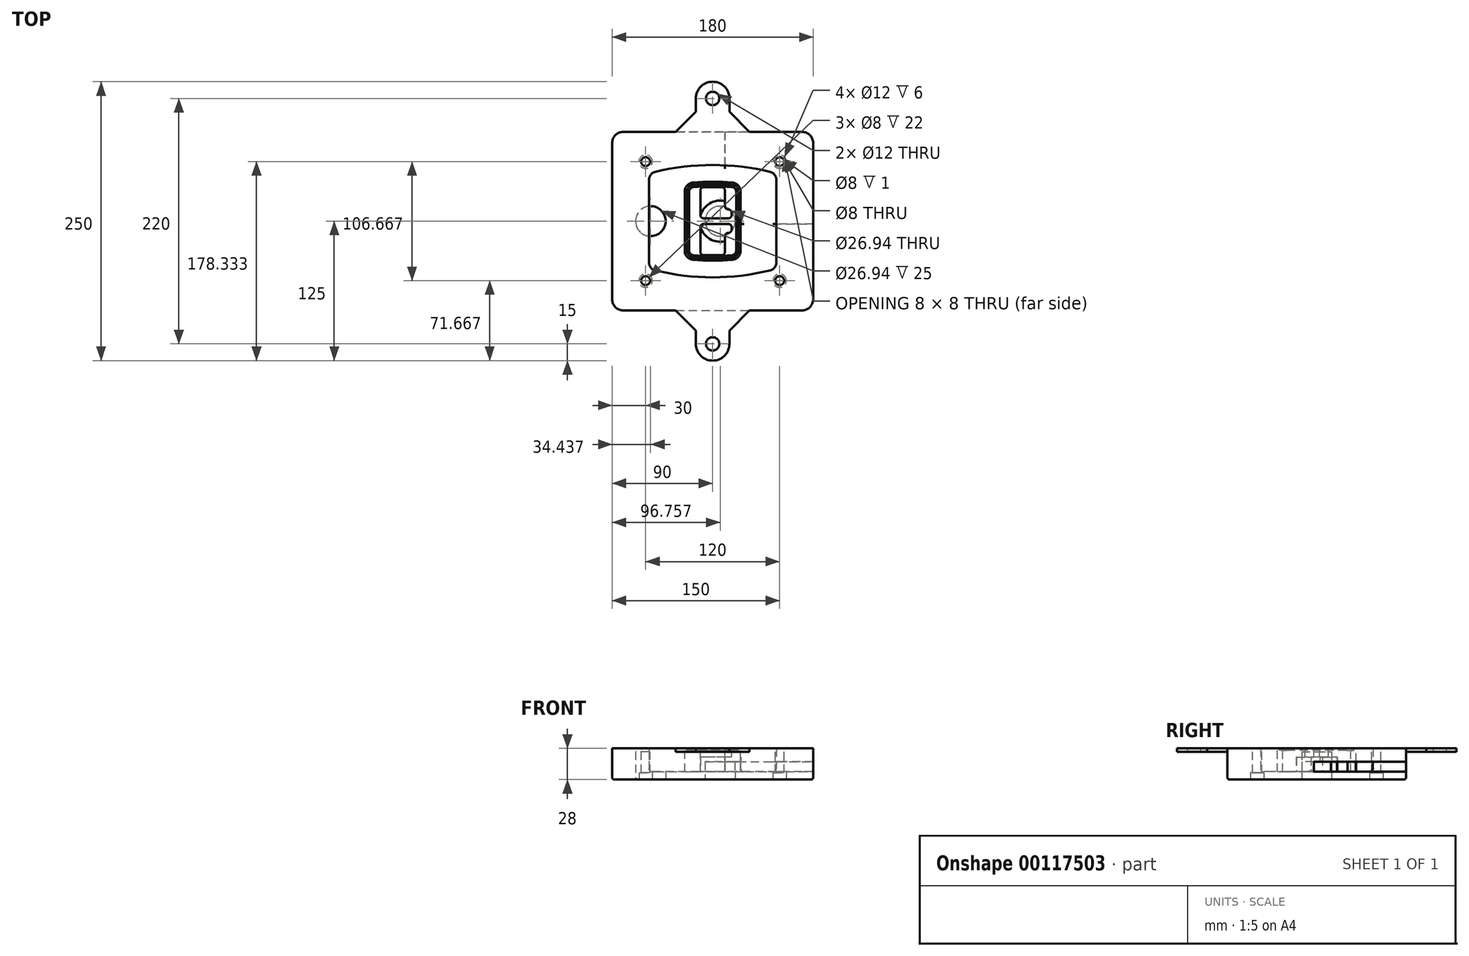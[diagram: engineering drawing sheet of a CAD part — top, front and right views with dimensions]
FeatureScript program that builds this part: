
annotation { "Feature Type Name" : "Feature", "Feature Type Description" : "" }
export const myFeature = defineFeature(function(context is Context, id is Id, definition is map)
    precondition{}
    {
        {
            var Q0;
            Q0=qCreatedBy(makeId("Top.planeOp"),FACE);
            var sketch = newSketch(context, id + "F0", { "sketchPlane" : qUnion([Q0])});
            skPoint(sketch, "E0.rect.middle", {"position": v(0, 0) * mm});
            skLineSegment(sketch, "E1.bottom", {"start": v(-80, -80) * mm, "end": v(80, -80) * mm});
            skLineSegment(sketch, "E1.top", {"start": v(-80, 80) * mm, "end": v(80, 80) * mm});
            skLineSegment(sketch, "E1.left", {"start": v(-90, -70) * mm, "end": v(-90, 70) * mm});
            skLineSegment(sketch, "E1.right", {"start": v(90, -70) * mm, "end": v(90, 70) * mm});
            skLineSegment(sketch, "E2", {"start": v(-90, 80) * mm, "end": v(90, -80) * mm, "construction": true});
            skLineSegment(sketch, "E3", {"start": v(90, 80) * mm, "end": v(-90, -80) * mm, "construction": true});
            skCircle(sketch, "E4", {"center": v(-60, 53.33) * mm, "radius": 4 * mm});
            skCircle(sketch, "E5", {"center": v(60, 53.33) * mm, "radius": 4 * mm});
            skCircle(sketch, "E6", {"center": v(60, -53.33) * mm, "radius": 4 * mm});
            skCircle(sketch, "E7", {"center": v(-60, -53.33) * mm, "radius": 4 * mm});
            skLineSegment(sketch, "E8", {"start": v(-60, 53.33) * mm, "end": v(60, 53.33) * mm, "construction": true});
            skLineSegment(sketch, "E9", {"start": v(60, 53.33) * mm, "end": v(60, -53.33) * mm, "construction": true});
            skLineSegment(sketch, "E10", {"start": v(60, -53.33) * mm, "end": v(-60, -53.33) * mm, "construction": true});
            skLineSegment(sketch, "E11", {"start": v(-60, -53.33) * mm, "end": v(-60, 53.33) * mm, "construction": true});
            skLineSegment(sketch, "E12", {"start": v(-60, 37.3) * mm, "end": v(-60, -37.3) * mm});
            skLineSegment(sketch, "E13", {"start": v(60, 37.3) * mm, "end": v(60, -37.3) * mm});
            skArc(sketch, "E14", {"start": v(52.38, 47.01) * mm, "mid": v(0, 53.33) * mm, "end": v(-52.38, 47.01) * mm});
            skArc(sketch, "E15", {"start": v(-52.38, -47.01) * mm, "mid": v(0, -53.33) * mm, "end": v(52.38, -47.01) * mm});
            skLineSegment(sketch, "E16", {"start": v(-60, 0) * mm, "end": v(60, 0) * mm, "construction": true});
            skPoint(sketch, "E17.visualSharp", {"position": v(-60, -45) * mm});
            skArc(sketch, "E17.filletArc", {"start": v(-60, -37.3) * mm, "mid": v(-57.87, -43.47) * mm, "end": v(-52.38, -47.01) * mm});
            skPoint(sketch, "E18.visualSharp", {"position": v(-60, 45) * mm});
            skArc(sketch, "E18.filletArc", {"start": v(-52.38, 47.01) * mm, "mid": v(-57.87, 43.47) * mm, "end": v(-60, 37.3) * mm});
            skPoint(sketch, "E19.visualSharp", {"position": v(60, 45) * mm});
            skArc(sketch, "E19.filletArc", {"start": v(60, 37.3) * mm, "mid": v(57.87, 43.47) * mm, "end": v(52.38, 47.01) * mm});
            skPoint(sketch, "E20.visualSharp", {"position": v(60, -45) * mm});
            skArc(sketch, "E20.filletArc", {"start": v(52.38, -47.01) * mm, "mid": v(57.87, -43.47) * mm, "end": v(60, -37.3) * mm});
            skPoint(sketch, "E21.visualSharp", {"position": v(-90, 80) * mm});
            skArc(sketch, "E21.filletArc", {"start": v(-80, 80) * mm, "mid": v(-87.07, 77.07) * mm, "end": v(-90, 70) * mm});
            skPoint(sketch, "E22.visualSharp", {"position": v(90, 80) * mm});
            skArc(sketch, "E22.filletArc", {"start": v(90, 70) * mm, "mid": v(87.07, 77.07) * mm, "end": v(80, 80) * mm});
            skPoint(sketch, "E23.visualSharp", {"position": v(90, -80) * mm});
            skArc(sketch, "E23.filletArc", {"start": v(80, -80) * mm, "mid": v(87.07, -77.07) * mm, "end": v(90, -70) * mm});
            skPoint(sketch, "E24.visualSharp", {"position": v(-90, -80) * mm});
            skArc(sketch, "E24.filletArc", {"start": v(-90, -70) * mm, "mid": v(-87.07, -77.07) * mm, "end": v(-80, -80) * mm});
            skArc(sketch, "E25.0", {"start": v(57, 37.3) * mm, "mid": v(55.5, 41.62) * mm, "end": v(51.67, 44.1) * mm});
            skLineSegment(sketch, "E25.1", {"start": v(57, 37.3) * mm, "end": v(57, -37.3) * mm});
            skArc(sketch, "E25.2", {"start": v(51.67, -44.1) * mm, "mid": v(55.5, -41.62) * mm, "end": v(57, -37.3) * mm});
            skArc(sketch, "E25.3", {"start": v(-51.67, -44.1) * mm, "mid": v(0, -50.33) * mm, "end": v(51.67, -44.1) * mm});
            skArc(sketch, "E25.4", {"start": v(-57, -37.3) * mm, "mid": v(-55.5, -41.62) * mm, "end": v(-51.67, -44.1) * mm});
            skArc(sketch, "E25.5", {"start": v(51.67, 44.1) * mm, "mid": v(0, 50.33) * mm, "end": v(-51.67, 44.1) * mm});
            skLineSegment(sketch, "E25.6", {"start": v(-57, 37.3) * mm, "end": v(-57, -37.3) * mm});
            skArc(sketch, "E25.7", {"start": v(-51.67, 44.1) * mm, "mid": v(-55.5, 41.62) * mm, "end": v(-57, 37.3) * mm});
            skArc(sketch, "E26.0", {"start": v(-53.33, 50.9) * mm, "mid": v(-61.01, 45.94) * mm, "end": v(-64, 37.3) * mm});
            skArc(sketch, "E26.1", {"start": v(53.33, 50.9) * mm, "mid": v(0, 57.33) * mm, "end": v(-53.33, 50.9) * mm});
            skArc(sketch, "E26.2", {"start": v(64, 37.3) * mm, "mid": v(61.01, 45.94) * mm, "end": v(53.33, 50.9) * mm});
            skLineSegment(sketch, "E26.3", {"start": v(64, 37.3) * mm, "end": v(64, -37.3) * mm});
            skArc(sketch, "E26.4", {"start": v(53.33, -50.9) * mm, "mid": v(61.01, -45.94) * mm, "end": v(64, -37.3) * mm});
            skLineSegment(sketch, "E26.5", {"start": v(-64, 37.3) * mm, "end": v(-64, -37.3) * mm});
            skArc(sketch, "E26.6", {"start": v(-53.33, -50.9) * mm, "mid": v(0, -57.33) * mm, "end": v(53.33, -50.9) * mm});
            skArc(sketch, "E26.7", {"start": v(-64, -37.3) * mm, "mid": v(-61.01, -45.94) * mm, "end": v(-53.33, -50.9) * mm});
            skSolve(sketch);
        }
        {
            var Q0;
            Q0=makeQuery(id+"F0.imprint","IMPRINT",FACE,{"disambiguationData":[TD([[makeQuery(id+"F0.imprint","IMPRINT",EDGE,{"derivedFrom":sQuery(id+"F0.wireOp",EDGE,"E1.bottom")}),1.0]])]});
            var Q1;
            Q1=makeQuery(id+"F0.imprint","IMPRINT",FACE,{"disambiguationData":[TD([[makeQuery(id+"F0.imprint","IMPRINT",EDGE,{"derivedFrom":sQuery(id+"F0.wireOp",EDGE,"E12")}),1.0]])]});
            var Q2;
            Q2=makeQuery(id+"F0.imprint","IMPRINT",FACE,{"disambiguationData":[TD([[makeQuery(id+"F0.imprint","IMPRINT",EDGE,{"derivedFrom":sQuery(id+"F0.wireOp",EDGE,"E25.0")}),1.0]])]});
            var Q3;
            Q3=makeQuery(id+"F0.imprint","IMPRINT",FACE,{"disambiguationData":[TD([[makeQuery(id+"F0.imprint","IMPRINT",EDGE,{"derivedFrom":sQuery(id+"F0.wireOp",EDGE,"E12")}),-1.0]])]});
            extrude(context, id + "F1", {"entities" : qUnion([Q0, Q1, Q2, Q3]), "oppositeDirection" : true, "depth" : 25 * mm});
        }
        {
            var Q0;
            Q0=makeQuery(id+"F0.imprint","IMPRINT",FACE,{"disambiguationData":[TD([[makeQuery(id+"F0.imprint","IMPRINT",EDGE,{"derivedFrom":sQuery(id+"F0.wireOp",EDGE,"E12")}),1.0]])]});
            extrude(context, id + "F2", {"entities" : qUnion([Q0]), "operationType" : NewBodyOperationType.ADD, "depth" : 3 * mm});
        }
        {
            var Q0;
            Q0=makeQuery(id+"F0.imprint","IMPRINT",FACE,{"disambiguationData":[TD([[makeQuery(id+"F0.imprint","IMPRINT",EDGE,{"derivedFrom":sQuery(id+"F0.wireOp",EDGE,"E25.0")}),1.0]])]});
            extrude(context, id + "F3", {"entities" : qUnion([Q0]), "operationType" : NewBodyOperationType.REMOVE, "oppositeDirection" : true, "depth" : 18 * mm});
        }
        {
            var Q0;
            Q0=makeQuery(id+"F2.opExtrude","CAP_FACE",FACE,{"disambiguationData":[OSD([sQuery(id+"F0.wireOp",EDGE,"E12"),sQuery(id+"F0.wireOp",EDGE,"E13"),sQuery(id+"F0.wireOp",EDGE,"E14"),sQuery(id+"F0.wireOp",EDGE,"E15"),sQuery(id+"F0.wireOp",EDGE,"E17.filletArc"),sQuery(id+"F0.wireOp",EDGE,"E18.filletArc"),sQuery(id+"F0.wireOp",EDGE,"E19.filletArc"),sQuery(id+"F0.wireOp",EDGE,"E20.filletArc"),sQuery(id+"F0.wireOp",EDGE,"E25.0"),sQuery(id+"F0.wireOp",EDGE,"E25.1"),sQuery(id+"F0.wireOp",EDGE,"E25.2"),sQuery(id+"F0.wireOp",EDGE,"E25.3"),sQuery(id+"F0.wireOp",EDGE,"E25.4"),sQuery(id+"F0.wireOp",EDGE,"E25.5"),sQuery(id+"F0.wireOp",EDGE,"E25.6"),sQuery(id+"F0.wireOp",EDGE,"E25.7")])],"isStart":false});
            var sketch = newSketch(context, id + "F4", { "sketchPlane" : qUnion([Q0])});
            skArc(sketch, "E27.0", {"start": v(-17.7, -34.56) * mm, "mid": v(0, -35.33) * mm, "end": v(17.7, -34.56) * mm});
            skArc(sketch, "E28.0", {"start": v(17.7, 34.56) * mm, "mid": v(0, 35.33) * mm, "end": v(-17.7, 34.56) * mm});
            skLineSegment(sketch, "E29", {"start": v(-25, 26.59) * mm, "end": v(-25, -26.59) * mm});
            skLineSegment(sketch, "E30", {"start": v(25, 26.59) * mm, "end": v(25, -26.59) * mm});
            skLineSegment(sketch, "E31", {"start": v(-25, 33.78) * mm, "end": v(25, 33.78) * mm, "construction": true});
            skLineSegment(sketch, "E32", {"start": v(-25, -33.78) * mm, "end": v(25, -33.78) * mm, "construction": true});
            skPoint(sketch, "E33.visualSharp", {"position": v(-25, 33.78) * mm});
            skArc(sketch, "E33.filletArc", {"start": v(-17.7, 34.56) * mm, "mid": v(-22.9, 32) * mm, "end": v(-25, 26.59) * mm});
            skPoint(sketch, "E34.visualSharp", {"position": v(25, 33.78) * mm});
            skArc(sketch, "E34.filletArc", {"start": v(25, 26.59) * mm, "mid": v(22.9, 32) * mm, "end": v(17.7, 34.56) * mm});
            skPoint(sketch, "E35.visualSharp", {"position": v(25, -33.78) * mm});
            skArc(sketch, "E35.filletArc", {"start": v(17.7, -34.56) * mm, "mid": v(22.9, -32) * mm, "end": v(25, -26.59) * mm});
            skPoint(sketch, "E36.visualSharp", {"position": v(-25, -33.78) * mm});
            skArc(sketch, "E36.filletArc", {"start": v(-25, -26.59) * mm, "mid": v(-22.9, -32) * mm, "end": v(-17.7, -34.56) * mm});
            skArc(sketch, "E37.0", {"start": v(51.67, 44.1) * mm, "mid": v(0, 50.33) * mm, "end": v(-51.67, 44.1) * mm});
            skArc(sketch, "E37.1", {"start": v(-51.67, 44.1) * mm, "mid": v(-55.5, 41.62) * mm, "end": v(-57, 37.3) * mm});
            skLineSegment(sketch, "E37.2", {"start": v(-57, 37.3) * mm, "end": v(-57, -37.3) * mm});
            skArc(sketch, "E37.3", {"start": v(-57, -37.3) * mm, "mid": v(-55.5, -41.62) * mm, "end": v(-51.67, -44.1) * mm});
            skArc(sketch, "E37.4", {"start": v(-51.67, -44.1) * mm, "mid": v(0, -50.33) * mm, "end": v(51.67, -44.1) * mm});
            skArc(sketch, "E37.5", {"start": v(51.67, -44.1) * mm, "mid": v(55.5, -41.62) * mm, "end": v(57, -37.3) * mm});
            skLineSegment(sketch, "E37.6", {"start": v(57, 37.3) * mm, "end": v(57, -37.3) * mm});
            skArc(sketch, "E37.7", {"start": v(57, 37.3) * mm, "mid": v(55.5, 41.62) * mm, "end": v(51.67, 44.1) * mm});
            skLineSegment(sketch, "E38.0", {"start": v(23, 26.59) * mm, "end": v(23, -26.59) * mm});
            skArc(sketch, "E38.1", {"start": v(17.53, -32.56) * mm, "mid": v(21.42, -30.64) * mm, "end": v(23, -26.59) * mm});
            skArc(sketch, "E38.2", {"start": v(-17.53, -32.56) * mm, "mid": v(0, -33.33) * mm, "end": v(17.53, -32.56) * mm});
            skArc(sketch, "E38.3", {"start": v(-23, -26.59) * mm, "mid": v(-21.42, -30.64) * mm, "end": v(-17.53, -32.56) * mm});
            skLineSegment(sketch, "E38.4", {"start": v(-23, 26.59) * mm, "end": v(-23, -26.59) * mm});
            skArc(sketch, "E38.5", {"start": v(23, 26.59) * mm, "mid": v(21.42, 30.64) * mm, "end": v(17.53, 32.56) * mm});
            skArc(sketch, "E38.6", {"start": v(-17.53, 32.56) * mm, "mid": v(-21.42, 30.64) * mm, "end": v(-23, 26.59) * mm});
            skArc(sketch, "E38.7", {"start": v(17.53, 32.56) * mm, "mid": v(0, 33.33) * mm, "end": v(-17.53, 32.56) * mm});
            skArc(sketch, "E39.0", {"start": v(21, 26.59) * mm, "mid": v(19.95, 29.29) * mm, "end": v(17.35, 30.57) * mm});
            skLineSegment(sketch, "E39.1", {"start": v(21, 26.59) * mm, "end": v(21, -26.59) * mm});
            skArc(sketch, "E39.2", {"start": v(17.35, -30.57) * mm, "mid": v(19.95, -29.29) * mm, "end": v(21, -26.59) * mm});
            skArc(sketch, "E39.3", {"start": v(-17.35, -30.57) * mm, "mid": v(0, -31.33) * mm, "end": v(17.35, -30.57) * mm});
            skArc(sketch, "E39.4", {"start": v(-21, -26.59) * mm, "mid": v(-19.95, -29.29) * mm, "end": v(-17.35, -30.57) * mm});
            skArc(sketch, "E39.5", {"start": v(17.35, 30.57) * mm, "mid": v(0, 31.33) * mm, "end": v(-17.35, 30.57) * mm});
            skLineSegment(sketch, "E39.6", {"start": v(-21, 26.59) * mm, "end": v(-21, -26.59) * mm});
            skArc(sketch, "E39.7", {"start": v(-17.35, 30.57) * mm, "mid": v(-19.95, 29.29) * mm, "end": v(-21, 26.59) * mm});
            skLineSegment(sketch, "E40", {"start": v(-25, 0) * mm, "end": v(25, 0) * mm, "construction": true});
            skLineSegment(sketch, "E41", {"start": v(-11, 5.5) * mm, "end": v(-11, 27.5) * mm});
            skLineSegment(sketch, "E42", {"start": v(-8, 30.5) * mm, "end": v(8, 30.5) * mm});
            skLineSegment(sketch, "E43", {"start": v(11, 27.5) * mm, "end": v(11, 13.5) * mm});
            skLineSegment(sketch, "E44", {"start": v(14, 10.5) * mm, "end": v(14, 10.5) * mm});
            skLineSegment(sketch, "E45", {"start": v(17, 7.5) * mm, "end": v(17, 5.5) * mm});
            skLineSegment(sketch, "E46", {"start": v(14, 2.5) * mm, "end": v(-8, 2.5) * mm});
            skPoint(sketch, "E47.visualSharp", {"position": v(-11, 30.5) * mm});
            skArc(sketch, "E47.filletArc", {"start": v(-8, 30.5) * mm, "mid": v(-10.12, 29.62) * mm, "end": v(-11, 27.5) * mm});
            skPoint(sketch, "E48.visualSharp", {"position": v(11, 30.5) * mm});
            skArc(sketch, "E48.filletArc", {"start": v(11, 27.5) * mm, "mid": v(10.12, 29.62) * mm, "end": v(8, 30.5) * mm});
            skPoint(sketch, "E49.visualSharp", {"position": v(11, 10.5) * mm});
            skArc(sketch, "E49.filletArc", {"start": v(11, 13.5) * mm, "mid": v(11.88, 11.38) * mm, "end": v(14, 10.5) * mm});
            skPoint(sketch, "E50.visualSharp", {"position": v(17, 10.5) * mm});
            skArc(sketch, "E50.filletArc", {"start": v(17, 7.5) * mm, "mid": v(16.12, 9.62) * mm, "end": v(14, 10.5) * mm});
            skPoint(sketch, "E51.visualSharp", {"position": v(17, 2.5) * mm});
            skArc(sketch, "E51.filletArc", {"start": v(14, 2.5) * mm, "mid": v(16.12, 3.38) * mm, "end": v(17, 5.5) * mm});
            skPoint(sketch, "E52.visualSharp", {"position": v(-11, 2.5) * mm});
            skArc(sketch, "E52.filletArc", {"start": v(-11, 5.5) * mm, "mid": v(-10.12, 3.38) * mm, "end": v(-8, 2.5) * mm});
            skLineSegment(sketch, "E53.0.MirrorCS", {"start": v(14, -2.5) * mm, "end": v(-8, -2.5) * mm});
            skArc(sketch, "E54.0.MirrorCS", {"start": v(-11, -5.5) * mm, "mid": v(-10.12, -3.38) * mm, "end": v(-8, -2.5) * mm});
            skLineSegment(sketch, "E55.0.MirrorCS", {"start": v(-11, -5.5) * mm, "end": v(-11, -27.5) * mm});
            skArc(sketch, "E56.0.MirrorCS", {"start": v(-8, -30.5) * mm, "mid": v(-10.12, -29.62) * mm, "end": v(-11, -27.5) * mm});
            skLineSegment(sketch, "E57.0.MirrorCS", {"start": v(-8, -30.5) * mm, "end": v(8, -30.5) * mm});
            skArc(sketch, "E58.0.MirrorCS", {"start": v(11, -27.5) * mm, "mid": v(10.12, -29.62) * mm, "end": v(8, -30.5) * mm});
            skLineSegment(sketch, "E59.0.MirrorCS", {"start": v(11, -27.5) * mm, "end": v(11, -13.5) * mm});
            skArc(sketch, "E60.0.MirrorCS", {"start": v(11, -13.5) * mm, "mid": v(11.88, -11.38) * mm, "end": v(14, -10.5) * mm});
            skArc(sketch, "E61.0.MirrorCS", {"start": v(17, -7.5) * mm, "mid": v(16.12, -9.62) * mm, "end": v(14, -10.5) * mm});
            skLineSegment(sketch, "E62.0.MirrorCS", {"start": v(17, -7.5) * mm, "end": v(17, -5.5) * mm});
            skArc(sketch, "E63.0.MirrorCS", {"start": v(14, -2.5) * mm, "mid": v(16.12, -3.38) * mm, "end": v(17, -5.5) * mm});
            skSolve(sketch);
        }
        {
            var Q0;
            Q0=makeQuery(id+"F4.imprint","IMPRINT",FACE,{"disambiguationData":[TD([[makeQuery(id+"F4.imprint","IMPRINT",EDGE,{"derivedFrom":sQuery(id+"F4.wireOp",EDGE,"E27.0")}),1.0]])]});
            var Q1;
            Q1=makeQuery(id+"F4.imprint","IMPRINT",FACE,{"disambiguationData":[TD([[makeQuery(id+"F4.imprint","IMPRINT",EDGE,{"derivedFrom":sQuery(id+"F4.wireOp",EDGE,"E38.0")}),-1.0]])]});
            var Q2;
            Q2=makeQuery(id+"F4.imprint","IMPRINT",FACE,{"disambiguationData":[TD([[makeQuery(id+"F4.imprint","IMPRINT",EDGE,{"derivedFrom":sQuery(id+"F4.wireOp",EDGE,"E39.0")}),1.0]])]});
            extrude(context, id + "F5", {"entities" : qUnion([Q0, Q1, Q2]), "operationType" : NewBodyOperationType.ADD, "endBound" : BoundingType.UP_TO_NEXT, "oppositeDirection" : true, "depth" : 25 * mm});
        }
        {
            var Q0;
            Q0=makeQuery(id+"F4.imprint","IMPRINT",FACE,{"disambiguationData":[TD([[makeQuery(id+"F4.imprint","IMPRINT",EDGE,{"derivedFrom":sQuery(id+"F4.wireOp",EDGE,"E38.0")}),-1.0]])]});
            extrude(context, id + "F6", {"entities" : qUnion([Q0]), "operationType" : NewBodyOperationType.REMOVE, "oppositeDirection" : true, "depth" : 2 * mm});
        }
        {
            var Q0;
            Q0=makeQuery(id+"F1.opExtrude","CAP_FACE",FACE,{"disambiguationData":[OSD([sQuery(id+"F0.wireOp",EDGE,"E1.bottom"),sQuery(id+"F0.wireOp",EDGE,"E1.top"),sQuery(id+"F0.wireOp",EDGE,"E1.left"),sQuery(id+"F0.wireOp",EDGE,"E1.right"),sQuery(id+"F0.wireOp",EDGE,"E4"),sQuery(id+"F0.wireOp",EDGE,"E5"),sQuery(id+"F0.wireOp",EDGE,"E6"),sQuery(id+"F0.wireOp",EDGE,"E7"),sQuery(id+"F0.wireOp",EDGE,"E21.filletArc"),sQuery(id+"F0.wireOp",EDGE,"E22.filletArc"),sQuery(id+"F0.wireOp",EDGE,"E23.filletArc"),sQuery(id+"F0.wireOp",EDGE,"E24.filletArc")])],"isStart":false});
            var sketch = newSketch(context, id + "F7", { "sketchPlane" : qUnion([Q0])});
            skCircle(sketch, "E64", {"center": v(6.76, 0) * mm, "radius": 13.47 * mm});
            skCircle(sketch, "E65", {"center": v(-55.56, 0) * mm, "radius": 13.47 * mm});
            skLineSegment(sketch, "E66", {"start": v(90, 0) * mm, "end": v(-90, 0) * mm});
            skCircle(sketch, "E67", {"center": v(6.76, 0) * mm, "radius": 18.47 * mm});
            skCircle(sketch, "E68", {"center": v(60, -53.33) * mm, "radius": 6 * mm});
            skCircle(sketch, "E69", {"center": v(-60, -53.33) * mm, "radius": 6 * mm});
            skCircle(sketch, "E70", {"center": v(-60, 53.33) * mm, "radius": 6 * mm});
            skCircle(sketch, "E71", {"center": v(60, 53.33) * mm, "radius": 6 * mm});
            skSolve(sketch);
        }
        {
            var Q0;
            {var subQ1=sQuery(id+"F7.wireOp",EDGE,"E66");var subQ4=sQuery(id+"F7.wireOp",EDGE,"E64");var subQ6=makeQuery(id+"F7.imprint","INTERSECT",VERTEX,{"disambiguationData":[OD(0.0)],"derivedFrom":[subQ4,subQ1]});Q0=makeQuery(id+"F7.imprint","IMPRINT",FACE,{"disambiguationData":[TD([[makeQuery(id+"F7.imprint","IMPRINT",EDGE,{"disambiguationData":[TD([[subQ6,-1.0]])],"derivedFrom":subQ4}),-1.0]])]});}
            var Q1;
            {var subQ0=sQuery(id+"F7.wireOp",EDGE,"E66");var subQ1=sQuery(id+"F7.wireOp",EDGE,"E64");var subQ3=makeQuery(id+"F7.imprint","INTERSECT",VERTEX,{"disambiguationData":[OD(0.0)],"derivedFrom":[subQ1,subQ0]});Q1=makeQuery(id+"F7.imprint","IMPRINT",FACE,{"disambiguationData":[TD([[makeQuery(id+"F7.imprint","IMPRINT",EDGE,{"disambiguationData":[TD([[subQ3,-1.0]])],"derivedFrom":subQ1}),1.0]])]});}
            var Q2;
            {var subQ0=sQuery(id+"F7.wireOp",EDGE,"E66");var subQ1=sQuery(id+"F7.wireOp",EDGE,"E64");var subQ3=makeQuery(id+"F7.imprint","INTERSECT",VERTEX,{"disambiguationData":[OD(0.0)],"derivedFrom":[subQ1,subQ0]});Q2=makeQuery(id+"F7.imprint","IMPRINT",FACE,{"disambiguationData":[TD([[makeQuery(id+"F7.imprint","IMPRINT",EDGE,{"disambiguationData":[TD([[subQ3,1.0]])],"derivedFrom":subQ1}),1.0]])]});}
            var Q3;
            {var subQ1=sQuery(id+"F7.wireOp",EDGE,"E66");var subQ4=sQuery(id+"F7.wireOp",EDGE,"E64");var subQ6=makeQuery(id+"F7.imprint","INTERSECT",VERTEX,{"disambiguationData":[OD(0.0)],"derivedFrom":[subQ4,subQ1]});Q3=makeQuery(id+"F7.imprint","IMPRINT",FACE,{"disambiguationData":[TD([[makeQuery(id+"F7.imprint","IMPRINT",EDGE,{"disambiguationData":[TD([[subQ6,1.0]])],"derivedFrom":subQ4}),-1.0]])]});}
            extrude(context, id + "F8", {"entities" : qUnion([Q0, Q1, Q2, Q3]), "operationType" : NewBodyOperationType.ADD, "oppositeDirection" : true, "depth" : 20 * mm});
        }
        {
            var Q0;
            {var subQ0=sQuery(id+"F7.wireOp",EDGE,"E66");var subQ1=sQuery(id+"F7.wireOp",EDGE,"E64");var subQ3=makeQuery(id+"F7.imprint","INTERSECT",VERTEX,{"disambiguationData":[OD(0.0)],"derivedFrom":[subQ1,subQ0]});Q0=makeQuery(id+"F7.imprint","IMPRINT",FACE,{"disambiguationData":[TD([[makeQuery(id+"F7.imprint","IMPRINT",EDGE,{"disambiguationData":[TD([[subQ3,-1.0]])],"derivedFrom":subQ1}),1.0]])]});}
            var Q1;
            {var subQ0=sQuery(id+"F7.wireOp",EDGE,"E66");var subQ1=sQuery(id+"F7.wireOp",EDGE,"E64");var subQ3=makeQuery(id+"F7.imprint","INTERSECT",VERTEX,{"disambiguationData":[OD(0.0)],"derivedFrom":[subQ1,subQ0]});Q1=makeQuery(id+"F7.imprint","IMPRINT",FACE,{"disambiguationData":[TD([[makeQuery(id+"F7.imprint","IMPRINT",EDGE,{"disambiguationData":[TD([[subQ3,1.0]])],"derivedFrom":subQ1}),1.0]])]});}
            extrude(context, id + "F9", {"entities" : qUnion([Q0, Q1]), "operationType" : NewBodyOperationType.REMOVE, "oppositeDirection" : true, "depth" : 16 * mm});
        }
        {
            var Q0;
            {var subQ0=sQuery(id+"F7.wireOp",EDGE,"E66");var subQ1=sQuery(id+"F7.wireOp",EDGE,"E65");var subQ3=makeQuery(id+"F7.imprint","INTERSECT",VERTEX,{"disambiguationData":[OD(0.0)],"derivedFrom":[subQ1,subQ0]});Q0=makeQuery(id+"F7.imprint","IMPRINT",FACE,{"disambiguationData":[TD([[makeQuery(id+"F7.imprint","IMPRINT",EDGE,{"disambiguationData":[TD([[subQ3,-1.0]])],"derivedFrom":subQ1}),1.0]])]});}
            var Q1;
            {var subQ0=sQuery(id+"F7.wireOp",EDGE,"E66");var subQ1=sQuery(id+"F7.wireOp",EDGE,"E65");var subQ3=makeQuery(id+"F7.imprint","INTERSECT",VERTEX,{"disambiguationData":[OD(0.0)],"derivedFrom":[subQ1,subQ0]});Q1=makeQuery(id+"F7.imprint","IMPRINT",FACE,{"disambiguationData":[TD([[makeQuery(id+"F7.imprint","IMPRINT",EDGE,{"disambiguationData":[TD([[subQ3,1.0]])],"derivedFrom":subQ1}),1.0]])]});}
            extrude(context, id + "F10", {"entities" : qUnion([Q0, Q1]), "operationType" : NewBodyOperationType.REMOVE, "oppositeDirection" : true, "depth" : 25 * mm});
        }
        {
            var Q0;
            Q0=makeQuery(id+"F7.imprint","IMPRINT",FACE,{"disambiguationData":[TD([[makeQuery(id+"F7.imprint","IMPRINT",EDGE,{"derivedFrom":sQuery(id+"F7.wireOp",EDGE,"E68")}),1.0]])]});
            var Q1;
            Q1=makeQuery(id+"F7.imprint","IMPRINT",FACE,{"disambiguationData":[TD([[makeQuery(id+"F7.imprint","IMPRINT",EDGE,{"derivedFrom":makeQuery(id+"F1.opExtrude","CAP_EDGE",EDGE,{"disambiguationData":[OSD([sQuery(id+"F0.wireOp",EDGE,"E5")])],"isStart":false})}),-1.0]])]});
            var Q2;
            Q2=makeQuery(id+"F7.imprint","IMPRINT",FACE,{"disambiguationData":[TD([[makeQuery(id+"F7.imprint","IMPRINT",EDGE,{"derivedFrom":sQuery(id+"F7.wireOp",EDGE,"E69")}),1.0]])]});
            var Q3;
            Q3=makeQuery(id+"F7.imprint","IMPRINT",FACE,{"disambiguationData":[TD([[makeQuery(id+"F7.imprint","IMPRINT",EDGE,{"derivedFrom":makeQuery(id+"F1.opExtrude","CAP_EDGE",EDGE,{"disambiguationData":[OSD([sQuery(id+"F0.wireOp",EDGE,"E4")])],"isStart":false})}),-1.0]])]});
            var Q4;
            Q4=makeQuery(id+"F7.imprint","IMPRINT",FACE,{"disambiguationData":[TD([[makeQuery(id+"F7.imprint","IMPRINT",EDGE,{"derivedFrom":sQuery(id+"F7.wireOp",EDGE,"E70")}),1.0]])]});
            var Q5;
            Q5=makeQuery(id+"F7.imprint","IMPRINT",FACE,{"disambiguationData":[TD([[makeQuery(id+"F7.imprint","IMPRINT",EDGE,{"derivedFrom":makeQuery(id+"F1.opExtrude","CAP_EDGE",EDGE,{"disambiguationData":[OSD([sQuery(id+"F0.wireOp",EDGE,"E7")])],"isStart":false})}),-1.0]])]});
            var Q6;
            Q6=makeQuery(id+"F7.imprint","IMPRINT",FACE,{"disambiguationData":[TD([[makeQuery(id+"F7.imprint","IMPRINT",EDGE,{"derivedFrom":sQuery(id+"F7.wireOp",EDGE,"E71")}),1.0]])]});
            var Q7;
            Q7=makeQuery(id+"F7.imprint","IMPRINT",FACE,{"disambiguationData":[TD([[makeQuery(id+"F7.imprint","IMPRINT",EDGE,{"derivedFrom":makeQuery(id+"F1.opExtrude","CAP_EDGE",EDGE,{"disambiguationData":[OSD([sQuery(id+"F0.wireOp",EDGE,"E6")])],"isStart":false})}),-1.0]])]});
            extrude(context, id + "F11", {"entities" : qUnion([Q0, Q1, Q2, Q3, Q4, Q5, Q6, Q7]), "operationType" : NewBodyOperationType.REMOVE, "oppositeDirection" : true, "depth" : 6 * mm});
        }
        {
            var Q0;
            Q0=makeQuery(id+"F9.boolean.opBoolean","COPY",FACE,{"derivedFrom":makeQuery(id+"F9.opExtrude","CAP_FACE",FACE,{"disambiguationData":[OSD([sQuery(id+"F7.wireOp",EDGE,"E64")])],"isStart":false})});
            var sketch = newSketch(context, id + "F12", { "sketchPlane" : qUnion([Q0])});
            skArc(sketch, "E72.0", {"start": v(11, -88.19) * mm, "mid": v(97.1, -83.6) * mm, "end": v(92.5, 2.5) * mm});
            skLineSegment(sketch, "E72.1", {"start": v(11, -17.97) * mm, "end": v(11, -17.97) * mm});
            skLineSegment(sketch, "E73", {"start": v(92.5, -105.13) * mm, "end": v(102.3, -105.13) * mm});
            skLineSegment(sketch, "E74.0", {"start": v(92.5, 2.5) * mm, "end": v(14, 2.5) * mm});
            skArc(sketch, "E74.1", {"start": v(14, 2.5) * mm, "mid": v(16.12, 3.38) * mm, "end": v(17, 5.5) * mm});
            skLineSegment(sketch, "E74.2", {"start": v(17, 7.5) * mm, "end": v(17, 5.5) * mm});
            skArc(sketch, "E74.3", {"start": v(17, 7.5) * mm, "mid": v(16.12, 9.62) * mm, "end": v(14, 10.5) * mm});
            skArc(sketch, "E74.4", {"start": v(11, 13.5) * mm, "mid": v(11.88, 11.38) * mm, "end": v(14, 10.5) * mm});
            skLineSegment(sketch, "E74.5", {"start": v(11, 13.5) * mm, "end": v(11, -88.19) * mm});
            skLineSegment(sketch, "E74.7", {"start": v(92.5, -2.5) * mm, "end": v(14, -2.5) * mm});
            skArc(sketch, "E74.8", {"start": v(14, -2.5) * mm, "mid": v(16.12, -3.38) * mm, "end": v(17, -5.5) * mm});
            skLineSegment(sketch, "E74.9", {"start": v(17, -7.5) * mm, "end": v(17, -5.5) * mm});
            skArc(sketch, "E74.10", {"start": v(17, -7.5) * mm, "mid": v(16.12, -9.62) * mm, "end": v(14, -10.5) * mm});
            skArc(sketch, "E74.11", {"start": v(11, -13.5) * mm, "mid": v(11.88, -11.38) * mm, "end": v(14, -10.5) * mm});
            skLineSegment(sketch, "E74.12", {"start": v(11, -17.97) * mm, "end": v(11, -13.5) * mm});
            skPoint(sketch, "E75.orphan", {"position": v(11, -27.5) * mm});
            skPoint(sketch, "E76.orphan", {"position": v(-8, -2.5) * mm});
            skPoint(sketch, "E77.orphan", {"position": v(-8, 2.5) * mm});
            skPoint(sketch, "E78.orphan", {"position": v(11, 27.5) * mm});
            skSolve(sketch);
        }
        {
            var Q0;
            {var subQ7=sQuery(id+"F12.wireOp",EDGE,"E72.0");var subQ14=sQuery(id+"F12.wireOp",EDGE,"E72.1");var subQ16=sQuery(id+"F12.wireOp",EDGE,"E74.1");var subQ18=sQuery(id+"F12.wireOp",EDGE,"E74.8");Q0=qUnion([makeQuery(id+"F12.imprint","IMPRINT",FACE,{"disambiguationData":[TD([[makeQuery(id+"F12.imprint","IMPRINT",EDGE,{"derivedFrom":subQ7}),1.0]])]}),makeQuery(id+"F12.imprint","IMPRINT",FACE,{"disambiguationData":[TD([[makeQuery(id+"F12.imprint","IMPRINT",EDGE,{"derivedFrom":subQ14}),1.0]])]}),makeQuery(id+"F12.imprint","IMPRINT",FACE,{"disambiguationData":[TD([[makeQuery(id+"F12.imprint","IMPRINT",EDGE,{"derivedFrom":subQ16}),1.0]])]}),makeQuery(id+"F12.imprint","IMPRINT",FACE,{"disambiguationData":[TD([[makeQuery(id+"F12.imprint","IMPRINT",EDGE,{"derivedFrom":subQ18}),-1.0]])]})]);}
            var Q1;
            Q1=makeQuery(id+"F5.boolean.opBoolean","SPLIT",FACE,{"disambiguationData":[TD([makeQuery(id+"F5.opExtrude","SWEPT_FACE",FACE,{"disambiguationData":[OSD([sQuery(id+"F4.wireOp",EDGE,"E41")])]})])],"derivedFrom":makeQuery(id+"F3.boolean.opBoolean","COPY",FACE,{"derivedFrom":makeQuery(id+"F3.opExtrude","CAP_FACE",FACE,{"disambiguationData":[OSD([sQuery(id+"F0.wireOp",EDGE,"E25.0"),sQuery(id+"F0.wireOp",EDGE,"E25.1"),sQuery(id+"F0.wireOp",EDGE,"E25.2"),sQuery(id+"F0.wireOp",EDGE,"E25.3"),sQuery(id+"F0.wireOp",EDGE,"E25.4"),sQuery(id+"F0.wireOp",EDGE,"E25.5"),sQuery(id+"F0.wireOp",EDGE,"E25.6"),sQuery(id+"F0.wireOp",EDGE,"E25.7")])],"isStart":false})})});
            extrude(context, id + "F13", {"entities" : qUnion([Q0]), "operationType" : NewBodyOperationType.REMOVE, "endBound" : BoundingType.UP_TO_SURFACE, "endBoundEntityFace" : qUnion([Q1]), "depth" : 25 * mm});
        }
        {
            var Q0;
            Q0=makeQuery(id+"F3.boolean.opBoolean","COPY",EDGE,{"derivedFrom":makeQuery(id+"F3.opExtrude","CAP_EDGE",EDGE,{"disambiguationData":[OSD([sQuery(id+"F0.wireOp",EDGE,"E25.6")])],"isStart":false})});
            var Q1;
            Q1=makeQuery(id+"F8.boolean.opBoolean","INTERSECT",EDGE,{"derivedFrom":[makeQuery(id+"F5.opExtrude","SWEPT_FACE",FACE,{"disambiguationData":[OSD([sQuery(id+"F4.wireOp",EDGE,"E30")])]}),makeQuery(id+"F8.opExtrude","CAP_FACE",FACE,{"disambiguationData":[OSD([sQuery(id+"F7.wireOp",EDGE,"E67")])],"isStart":false})]});
            var Q2;
            Q2=makeQuery(id+"F8.boolean.opBoolean","INTERSECT",EDGE,{"disambiguationData":[OD(1.0)],"derivedFrom":[makeQuery(id+"F5.opExtrude","SWEPT_FACE",FACE,{"disambiguationData":[OSD([sQuery(id+"F4.wireOp",EDGE,"E30")])]}),makeQuery(id+"F8.opExtrude","SWEPT_FACE",FACE,{"disambiguationData":[OSD([sQuery(id+"F7.wireOp",EDGE,"E67")])]})]});
            var Q3;
            {var subQ0=makeQuery(id+"F3.boolean.opBoolean","COPY",FACE,{"derivedFrom":makeQuery(id+"F3.opExtrude","CAP_FACE",FACE,{"disambiguationData":[OSD([sQuery(id+"F0.wireOp",EDGE,"E25.0"),sQuery(id+"F0.wireOp",EDGE,"E25.1"),sQuery(id+"F0.wireOp",EDGE,"E25.2"),sQuery(id+"F0.wireOp",EDGE,"E25.3"),sQuery(id+"F0.wireOp",EDGE,"E25.4"),sQuery(id+"F0.wireOp",EDGE,"E25.5"),sQuery(id+"F0.wireOp",EDGE,"E25.6"),sQuery(id+"F0.wireOp",EDGE,"E25.7")])],"isStart":false})});var subQ1=sQuery(id+"F4.wireOp",EDGE,"E30");Q3=makeQuery(id+"F8.boolean.opBoolean","SPLIT",EDGE,{"disambiguationData":[TD([makeQuery(id+"F5.opExtrude","SWEPT_FACE",FACE,{"disambiguationData":[OSD([sQuery(id+"F4.wireOp",EDGE,"E35.filletArc")])]})])],"derivedFrom":makeQuery(id+"F5.opExtrude","TWEAK_EDGE",EDGE,{"derivedFrom":[subQ0,makeQuery(id+"F4.imprint","IMPRINT",EDGE,{"derivedFrom":subQ1})]})});}
            var Q4;
            {var subQ0=sQuery(id+"F0.wireOp",EDGE,"E25.0");var subQ1=sQuery(id+"F0.wireOp",EDGE,"E25.1");var subQ2=sQuery(id+"F0.wireOp",EDGE,"E25.2");var subQ3=sQuery(id+"F0.wireOp",EDGE,"E25.3");var subQ4=sQuery(id+"F0.wireOp",EDGE,"E25.4");var subQ5=sQuery(id+"F0.wireOp",EDGE,"E25.5");var subQ6=sQuery(id+"F0.wireOp",EDGE,"E25.6");var subQ7=sQuery(id+"F0.wireOp",EDGE,"E25.7");Q4=makeQuery(id+"F8.boolean.opBoolean","INTERSECT",EDGE,{"derivedFrom":[makeQuery(id+"F5.boolean.opBoolean","SPLIT",FACE,{"disambiguationData":[TD([makeQuery(id+"F2.opExtrude","SWEPT_FACE",FACE,{"disambiguationData":[OSD([subQ0])]})])],"derivedFrom":makeQuery(id+"F3.boolean.opBoolean","COPY",FACE,{"derivedFrom":makeQuery(id+"F3.opExtrude","CAP_FACE",FACE,{"disambiguationData":[OSD([subQ0,subQ1,subQ2,subQ3,subQ4,subQ5,subQ6,subQ7])],"isStart":false})})}),makeQuery(id+"F8.opExtrude","SWEPT_FACE",FACE,{"disambiguationData":[OSD([sQuery(id+"F7.wireOp",EDGE,"E67")])]})]});}
            var Q5;
            Q5=makeQuery(id+"F8.boolean.opBoolean","INTERSECT",EDGE,{"disambiguationData":[OD(0.0)],"derivedFrom":[makeQuery(id+"F5.opExtrude","SWEPT_FACE",FACE,{"disambiguationData":[OSD([sQuery(id+"F4.wireOp",EDGE,"E30")])]}),makeQuery(id+"F8.opExtrude","SWEPT_FACE",FACE,{"disambiguationData":[OSD([sQuery(id+"F7.wireOp",EDGE,"E67")])]})]});
            fillet(context, id + "F14", {"entities" : qUnion([Q0, Q1, Q2, Q3, Q4, Q5]), "radius" : 3 * mm, "tangentPropagation" : true, "allowEdgeOverflow" : false});
        }
        {
            var Q0;
            Q0=makeQuery(id+"F1.opExtrude","CAP_EDGE",EDGE,{"disambiguationData":[OSD([sQuery(id+"F0.wireOp",EDGE,"E1.bottom")])],"isStart":false});
            fillet(context, id + "F15", {"entities" : qUnion([Q0]), "radius" : 2 * mm, "tangentPropagation" : true, "allowEdgeOverflow" : false});
        }
        {
            var Q0;
            {var subQ0=sQuery(id+"F0.wireOp",EDGE,"E22.filletArc");var subQ1=sQuery(id+"F0.wireOp",EDGE,"E7");var subQ2=sQuery(id+"F0.wireOp",EDGE,"E6");var subQ3=sQuery(id+"F0.wireOp",EDGE,"E5");var subQ4=sQuery(id+"F0.wireOp",EDGE,"E4");var subQ5=sQuery(id+"F0.wireOp",EDGE,"E1.bottom");var subQ6=sQuery(id+"F0.wireOp",EDGE,"E21.filletArc");var subQ7=sQuery(id+"F0.wireOp",EDGE,"E1.top");var subQ8=sQuery(id+"F0.wireOp",EDGE,"E1.left");var subQ9=sQuery(id+"F0.wireOp",EDGE,"E1.right");var subQ10=sQuery(id+"F0.wireOp",EDGE,"E23.filletArc");var subQ11=sQuery(id+"F0.wireOp",EDGE,"E24.filletArc");Q0=makeQuery(id+"F2.boolean.opBoolean","SPLIT",FACE,{"disambiguationData":[TD([makeQuery(id+"F1.opExtrude","SWEPT_FACE",FACE,{"disambiguationData":[OSD([subQ5])]})])],"derivedFrom":makeQuery(id+"F1.opExtrude","CAP_FACE",FACE,{"disambiguationData":[OSD([subQ5,subQ7,subQ8,subQ9,subQ4,subQ3,subQ2,subQ1,subQ6,subQ0,subQ10,subQ11])],"isStart":true})});}
            var sketch = newSketch(context, id + "F16", { "sketchPlane" : qUnion([Q0])});
            skLineSegment(sketch, "E79.0", {"start": v(-90, -70) * mm, "end": v(-90, 70) * mm});
            skArc(sketch, "E79.1", {"start": v(-80, 80) * mm, "mid": v(-87.07, 77.07) * mm, "end": v(-90, 70) * mm});
            skLineSegment(sketch, "E79.2", {"start": v(-80, 80) * mm, "end": v(80, 80) * mm});
            skArc(sketch, "E79.3", {"start": v(90, 70) * mm, "mid": v(87.07, 77.07) * mm, "end": v(80, 80) * mm});
            skLineSegment(sketch, "E79.4", {"start": v(90, -70) * mm, "end": v(90, 70) * mm});
            skArc(sketch, "E79.5", {"start": v(80, -80) * mm, "mid": v(87.07, -77.07) * mm, "end": v(90, -70) * mm});
            skLineSegment(sketch, "E79.6", {"start": v(-80, -80) * mm, "end": v(80, -80) * mm});
            skArc(sketch, "E79.7", {"start": v(-90, -70) * mm, "mid": v(-87.07, -77.07) * mm, "end": v(-80, -80) * mm});
            skLineSegment(sketch, "E79.8", {"start": v(-60, 37.3) * mm, "end": v(-60, -37.3) * mm});
            skArc(sketch, "E79.9", {"start": v(-52.38, 47.01) * mm, "mid": v(-57.87, 43.47) * mm, "end": v(-60, 37.3) * mm});
            skArc(sketch, "E79.10", {"start": v(52.38, 47.01) * mm, "mid": v(0, 53.33) * mm, "end": v(-52.38, 47.01) * mm});
            skArc(sketch, "E79.11", {"start": v(60, 37.3) * mm, "mid": v(57.87, 43.47) * mm, "end": v(52.38, 47.01) * mm});
            skLineSegment(sketch, "E79.12", {"start": v(60, 37.3) * mm, "end": v(60, -37.3) * mm});
            skArc(sketch, "E79.13", {"start": v(52.38, -47.01) * mm, "mid": v(57.87, -43.47) * mm, "end": v(60, -37.3) * mm});
            skArc(sketch, "E79.14", {"start": v(-52.38, -47.01) * mm, "mid": v(0, -53.33) * mm, "end": v(52.38, -47.01) * mm});
            skArc(sketch, "E79.15", {"start": v(-60, -37.3) * mm, "mid": v(-57.87, -43.47) * mm, "end": v(-52.38, -47.01) * mm});
            skCircle(sketch, "E79.16", {"center": v(-60, -53.33) * mm, "radius": 4 * mm});
            skCircle(sketch, "E79.17", {"center": v(-60, 53.33) * mm, "radius": 4 * mm});
            skCircle(sketch, "E79.18", {"center": v(60, 53.33) * mm, "radius": 4 * mm});
            skCircle(sketch, "E79.19", {"center": v(60, -53.33) * mm, "radius": 4 * mm});
            skLineSegment(sketch, "E80", {"start": v(-15, 98) * mm, "end": v(-15, 110) * mm});
            skArc(sketch, "E81", {"start": v(-15, 110) * mm, "mid": v(0, 125) * mm, "end": v(15, 110) * mm});
            skLineSegment(sketch, "E82", {"start": v(0, 80) * mm, "end": v(0, 110) * mm, "construction": true});
            skCircle(sketch, "E83", {"center": v(0, 110) * mm, "radius": 6 * mm});
            skLineSegment(sketch, "E84", {"start": v(15, 110) * mm, "end": v(15, 98) * mm});
            skLineSegment(sketch, "E85", {"start": v(15, 98) * mm, "end": v(33, 80) * mm});
            skLineSegment(sketch, "E86", {"start": v(-15, 98) * mm, "end": v(-33, 80) * mm});
            skLineSegment(sketch, "E87", {"start": v(-90, 0) * mm, "end": v(90, 0) * mm, "construction": true});
            skCircle(sketch, "E88.MirrorC", {"center": v(0, -110) * mm, "radius": 6 * mm});
            skArc(sketch, "E89.MirrorCS", {"start": v(-15, -110) * mm, "mid": v(0, -125) * mm, "end": v(15, -110) * mm});
            skLineSegment(sketch, "E90.MirrorCS", {"start": v(-15, -98) * mm, "end": v(-33, -80) * mm});
            skLineSegment(sketch, "E91.MirrorCS", {"start": v(15, -98) * mm, "end": v(33, -80) * mm});
            skLineSegment(sketch, "E92.MirrorCS", {"start": v(15, -110) * mm, "end": v(15, -98) * mm});
            skLineSegment(sketch, "E93.MirrorCS", {"start": v(0, -80) * mm, "end": v(0, -110) * mm, "construction": true});
            skLineSegment(sketch, "E94.MirrorCS", {"start": v(-15, -98) * mm, "end": v(-15, -110) * mm});
            skSolve(sketch);
        }
        {
            var Q0;
            Q0 = qSketchRegion(id + "F16", true);
            var Q1;
            Q1=makeQuery(id+"F2.opExtrude","CAP_FACE",FACE,{"disambiguationData":[OSD([sQuery(id+"F0.wireOp",EDGE,"E12"),sQuery(id+"F0.wireOp",EDGE,"E13"),sQuery(id+"F0.wireOp",EDGE,"E14"),sQuery(id+"F0.wireOp",EDGE,"E15"),sQuery(id+"F0.wireOp",EDGE,"E17.filletArc"),sQuery(id+"F0.wireOp",EDGE,"E18.filletArc"),sQuery(id+"F0.wireOp",EDGE,"E19.filletArc"),sQuery(id+"F0.wireOp",EDGE,"E20.filletArc"),sQuery(id+"F0.wireOp",EDGE,"E25.0"),sQuery(id+"F0.wireOp",EDGE,"E25.1"),sQuery(id+"F0.wireOp",EDGE,"E25.2"),sQuery(id+"F0.wireOp",EDGE,"E25.3"),sQuery(id+"F0.wireOp",EDGE,"E25.4"),sQuery(id+"F0.wireOp",EDGE,"E25.5"),sQuery(id+"F0.wireOp",EDGE,"E25.6"),sQuery(id+"F0.wireOp",EDGE,"E25.7")])],"isStart":false});
            extrude(context, id + "F17", {"entities" : qUnion([Q0]), "operationType" : NewBodyOperationType.ADD, "endBound" : BoundingType.UP_TO_SURFACE, "endBoundEntityFace" : qUnion([Q1]), "depth" : 25 * mm});
        }
    });
